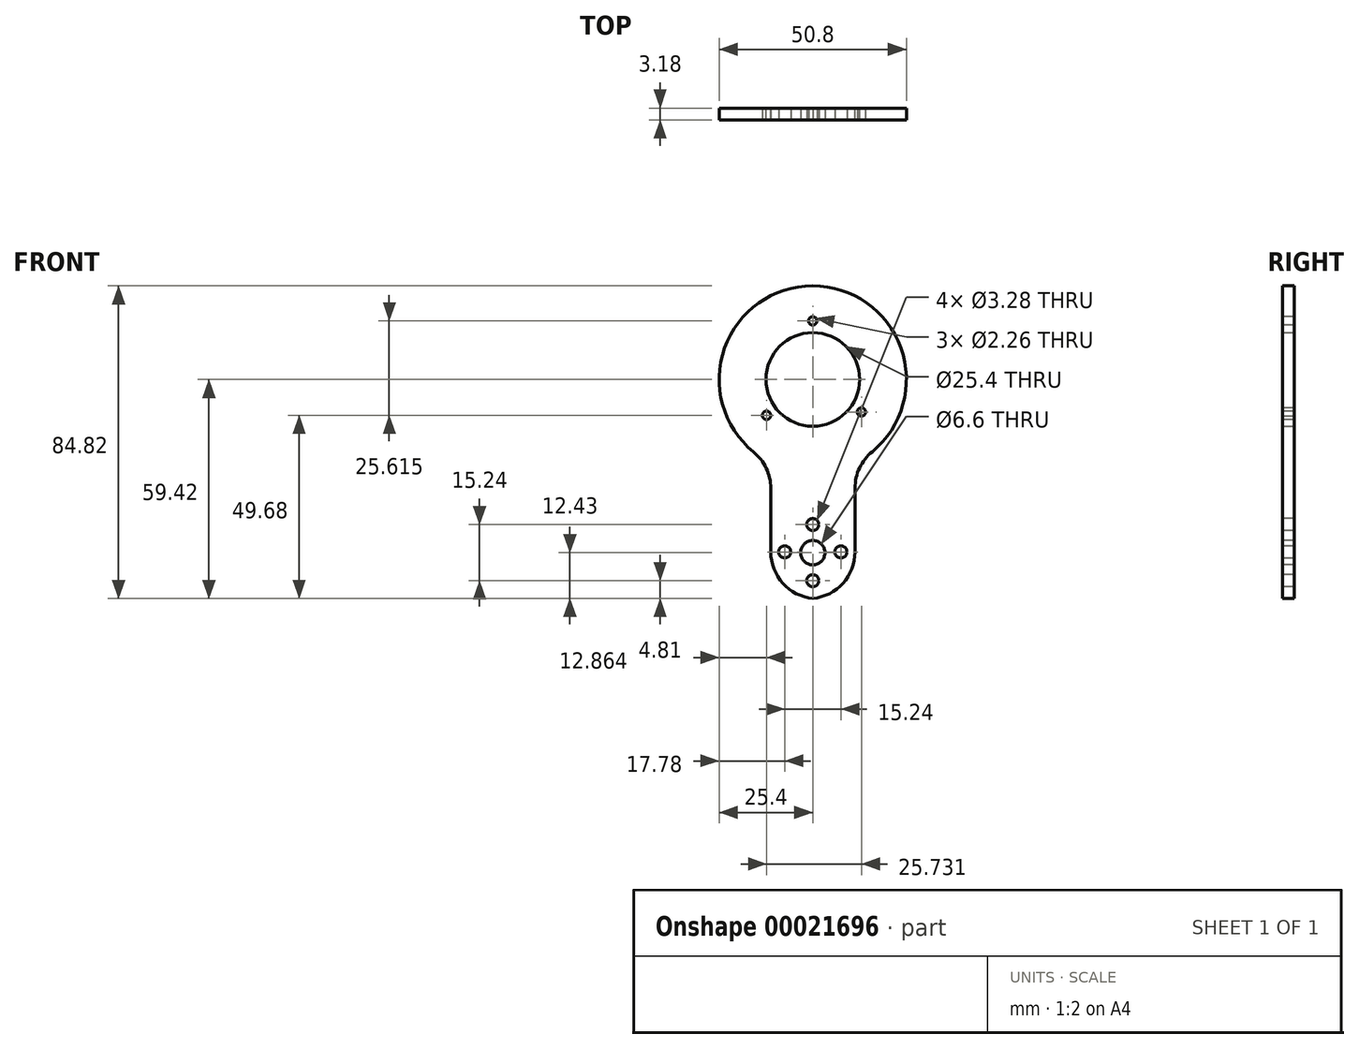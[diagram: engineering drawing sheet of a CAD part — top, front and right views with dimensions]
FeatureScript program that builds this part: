
annotation { "Feature Type Name" : "Feature", "Feature Type Description" : "" }
export const myFeature = defineFeature(function(context is Context, id is Id, definition is map)
    precondition{}
    {
        {
            var Q0;
            Q0=qCreatedBy(makeId("Front.planeOp"),FACE);
            var sketch = newSketch(context, id + "F0", { "sketchPlane" : qUnion([Q0])});
            skArc(sketch, "E0", {"start": v(11.47, -22.66) * mm, "mid": v(-0.04, 25.4) * mm, "end": v(-11.4, -22.7) * mm});
            skLineSegment(sketch, "E1.top", {"start": v(-11.4, -59.49) * mm, "end": v(11.47, -59.49) * mm});
            skLineSegment(sketch, "E1.left", {"start": v(-11.4, -22.7) * mm, "end": v(-11.4, -59.49) * mm});
            skLineSegment(sketch, "E1.right", {"start": v(11.47, -22.66) * mm, "end": v(11.47, -59.49) * mm});
            skCircle(sketch, "E2", {"center": v(0, 0) * mm, "radius": 12.7 * mm});
            skLineSegment(sketch, "E3", {"start": v(-11.4, -22.7) * mm, "end": v(70.16, -22.66) * mm, "construction": true});
            skSolve(sketch);
        }
        {
            var Q0;
            Q0=makeQuery(id+"F0.imprint","IMPRINT",FACE,{"disambiguationData":[TD([[makeQuery(id+"F0.imprint","IMPRINT",EDGE,{"derivedFrom":sQuery(id+"F0.wireOp",EDGE,"E0")}),1.0]])]});
            extrude(context, id + "F1", {"entities" : qUnion([Q0]), "depth" : 3.17 * mm});
        }
        {
            var Q0;
            Q0=makeQuery(id+"F1.opExtrude","CAP_FACE",FACE,{"disambiguationData":[OSD([sQuery(id+"F0.wireOp",EDGE,"E0"),sQuery(id+"F0.wireOp",EDGE,"E1.top"),sQuery(id+"F0.wireOp",EDGE,"E1.left"),sQuery(id+"F0.wireOp",EDGE,"E1.right"),sQuery(id+"F0.wireOp",EDGE,"E2"),sQuery(id+"F0.wireOp",EDGE,"88940b38-a4d3-4285-9d7f-f316f2c4ca14")])],"isStart":false});
            var sketch = newSketch(context, id + "F2", { "sketchPlane" : qUnion([Q0])});
            skPoint(sketch, "E4", {"position": v(0, 15.88) * mm});
            skPoint(sketch, "E5", {"position": v(13.2, -8.83) * mm});
            skPoint(sketch, "E6", {"position": v(-12.54, -9.74) * mm});
            skSolve(sketch);
        }
        {
            var Q0;
            Q0=sQuery(id+"F2.wireOp",VERTEX,"E4");
            var Q1;
            Q1=sQuery(id+"F2.wireOp",VERTEX,"E5");
            var Q2;
            Q2=sQuery(id+"F2.wireOp",VERTEX,"E6");
            var Q3;
            Q3=makeQuery(id+"F1.opExtrude","SWEPT_BODY",BODY,{"disambiguationData":[OSD([sQuery(id+"F0.wireOp",EDGE,"E0"),sQuery(id+"F0.wireOp",EDGE,"E1.top"),sQuery(id+"F0.wireOp",EDGE,"E1.left"),sQuery(id+"F0.wireOp",EDGE,"E1.right"),sQuery(id+"F0.wireOp",EDGE,"E2"),sQuery(id+"F0.wireOp",EDGE,"88940b38-a4d3-4285-9d7f-f316f2c4ca14")])]});
            hole(context, id + "F3", {"style" : HoleStyle.SIMPLE, "holeDiameter" : 2.26 * mm, "endStyle" : HoleEndStyle.THROUGH, "locations" : qUnion([Q0, Q1, Q2]), "scope" : qUnion([Q3])});
        }
        {
            var Q0;
            Q0=makeQuery(id+"F1.opExtrude","SWEPT_EDGE",EDGE,{"disambiguationData":[OSD([sQuery(id+"F0.wireOp",EDGE,"E0"),sQuery(id+"F0.wireOp",EDGE,"E1.left")])]});
            var Q1;
            Q1=makeQuery(id+"F1.opExtrude","SWEPT_EDGE",EDGE,{"disambiguationData":[OSD([sQuery(id+"F0.wireOp",EDGE,"E0"),sQuery(id+"F0.wireOp",EDGE,"E1.right")])]});
            fillet(context, id + "F4", {"entities" : qUnion([Q0, Q1]), "radius" : 12.7 * mm, "tangentPropagation" : true, "allowEdgeOverflow" : false});
        }
        {
            var Q0;
            Q0=makeQuery(id+"F1.opExtrude","CAP_FACE",FACE,{"disambiguationData":[OSD([sQuery(id+"F0.wireOp",EDGE,"E0"),sQuery(id+"F0.wireOp",EDGE,"E1.top"),sQuery(id+"F0.wireOp",EDGE,"E1.left"),sQuery(id+"F0.wireOp",EDGE,"E1.right"),sQuery(id+"F0.wireOp",EDGE,"E2"),sQuery(id+"F0.wireOp",EDGE,"88940b38-a4d3-4285-9d7f-f316f2c4ca14")])],"isStart":false});
            var sketch = newSketch(context, id + "F5", { "sketchPlane" : qUnion([Q0])});
            skCircle(sketch, "E7", {"center": v(0, -47) * mm, "radius": 3.3 * mm});
            skSolve(sketch);
        }
        {
            var Q0;
            Q0=sQuery(id+"F5.wireOp",VERTEX,"E7.center");
            var Q1;
            Q1=makeQuery(id+"F1.opExtrude","SWEPT_BODY",BODY,{"disambiguationData":[OSD([sQuery(id+"F0.wireOp",EDGE,"E0"),sQuery(id+"F0.wireOp",EDGE,"E1.top"),sQuery(id+"F0.wireOp",EDGE,"E1.left"),sQuery(id+"F0.wireOp",EDGE,"E1.right"),sQuery(id+"F0.wireOp",EDGE,"E2")])]});
            hole(context, id + "F6", {"style" : HoleStyle.SIMPLE, "holeDiameter" : 6.6 * mm, "endStyle" : HoleEndStyle.THROUGH, "locations" : qUnion([Q0]), "scope" : qUnion([Q1])});
        }
        {
            var Q0;
            Q0=makeQuery(id+"F1.opExtrude","SWEPT_EDGE",EDGE,{"disambiguationData":[OSD([sQuery(id+"F0.wireOp",EDGE,"E1.top"),sQuery(id+"F0.wireOp",EDGE,"E1.right")])]});
            var Q1;
            Q1=makeQuery(id+"F1.opExtrude","SWEPT_EDGE",EDGE,{"disambiguationData":[OSD([sQuery(id+"F0.wireOp",EDGE,"E1.top"),sQuery(id+"F0.wireOp",EDGE,"E1.left")])]});
            fillet(context, id + "F7", {"entities" : qUnion([Q0, Q1]), "radius" : 12.7 * mm, "tangentPropagation" : true, "allowEdgeOverflow" : false});
        }
        {
            var Q0;
            Q0=makeQuery(id+"F1.opExtrude","CAP_FACE",FACE,{"disambiguationData":[OSD([sQuery(id+"F0.wireOp",EDGE,"E0"),sQuery(id+"F0.wireOp",EDGE,"E1.top"),sQuery(id+"F0.wireOp",EDGE,"E1.left"),sQuery(id+"F0.wireOp",EDGE,"E1.right"),sQuery(id+"F0.wireOp",EDGE,"E2")])],"isStart":false});
            var sketch = newSketch(context, id + "F8", { "sketchPlane" : qUnion([Q0])});
            skPoint(sketch, "E8", {"position": v(7.62, -46.79) * mm});
            skPoint(sketch, "E9", {"position": v(0, -39.37) * mm});
            skPoint(sketch, "E10", {"position": v(-7.62, -46.79) * mm});
            skPoint(sketch, "E11", {"position": v(0, -54.61) * mm});
            skPoint(sketch, "E12", {"position": v(0, -47) * mm});
            skSolve(sketch);
        }
        {
            var Q0;
            Q0=sQuery(id+"F8.wireOp",VERTEX,"E9");
            var Q1;
            Q1=sQuery(id+"F8.wireOp",VERTEX,"E8");
            var Q2;
            Q2=sQuery(id+"F8.wireOp",VERTEX,"E11");
            var Q3;
            Q3=sQuery(id+"F8.wireOp",VERTEX,"E10");
            var Q4;
            Q4=makeQuery(id+"F1.opExtrude","SWEPT_BODY",BODY,{"disambiguationData":[OSD([sQuery(id+"F0.wireOp",EDGE,"E0"),sQuery(id+"F0.wireOp",EDGE,"E1.top"),sQuery(id+"F0.wireOp",EDGE,"E1.left"),sQuery(id+"F0.wireOp",EDGE,"E1.right"),sQuery(id+"F0.wireOp",EDGE,"E2")])]});
            hole(context, id + "F9", {"style" : HoleStyle.SIMPLE, "holeDiameter" : 3.28 * mm, "endStyle" : HoleEndStyle.THROUGH, "locations" : qUnion([Q0, Q1, Q2, Q3]), "scope" : qUnion([Q4])});
        }
    });
